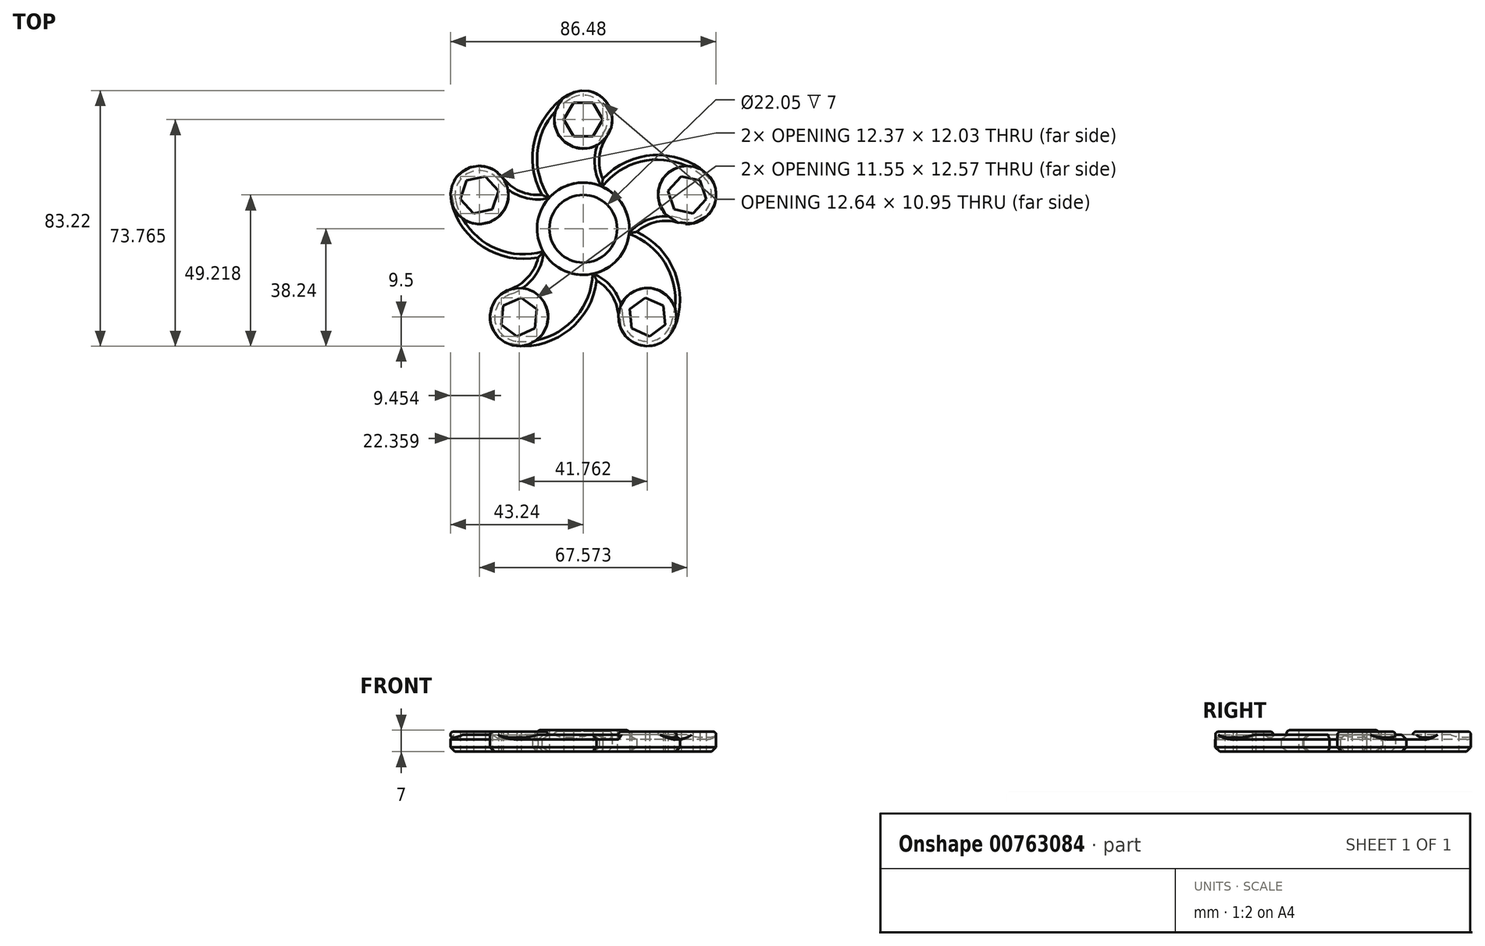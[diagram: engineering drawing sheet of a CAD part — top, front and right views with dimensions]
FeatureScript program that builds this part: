
annotation { "Feature Type Name" : "Feature", "Feature Type Description" : "" }
export const myFeature = defineFeature(function(context is Context, id is Id, definition is map)
    precondition{}
    {
        {
            var Q0;
            Q0=qCreatedBy(makeId("Top.planeOp"),FACE);
            var sketch = newSketch(context, id + "F0", { "sketchPlane" : qUnion([Q0])});
            skCircle(sketch, "E0", {"center": v(0, 0) * mm, "radius": 11.03 * mm});
            skCircle(sketch, "E1", {"center": v(0, 0) * mm, "radius": 15 * mm});
            skCircle(sketch, "E2.cCircle", {"center": v(0, 35.52) * mm, "radius": 5.47 * mm, "construction": true});
            skLineSegment(sketch, "E2.0", {"start": v(3.16, 30.05) * mm, "end": v(-3.16, 30.05) * mm});
            skLineSegment(sketch, "E2.1", {"start": v(-3.16, 30.05) * mm, "end": v(-6.32, 35.52) * mm});
            skLineSegment(sketch, "E2.2", {"start": v(-6.32, 35.52) * mm, "end": v(-3.16, 41) * mm});
            skLineSegment(sketch, "E2.3", {"start": v(-3.16, 41) * mm, "end": v(3.16, 41) * mm});
            skLineSegment(sketch, "E2.4", {"start": v(3.16, 41) * mm, "end": v(6.32, 35.52) * mm});
            skLineSegment(sketch, "E2.5", {"start": v(6.32, 35.52) * mm, "end": v(3.16, 30.05) * mm});
            skPoint(sketch, "E2.0.midPoint", {"position": v(0, 30.05) * mm});
            skCircle(sketch, "E3.1.0", {"center": v(33.79, 10.98) * mm, "radius": 5.47 * mm, "construction": true});
            skLineSegment(sketch, "E3.1.1", {"start": v(38.02, 15.68) * mm, "end": v(39.97, 9.66) * mm});
            skLineSegment(sketch, "E3.1.2", {"start": v(39.97, 9.66) * mm, "end": v(35.74, 4.97) * mm});
            skLineSegment(sketch, "E3.1.3", {"start": v(35.74, 4.97) * mm, "end": v(29.56, 6.28) * mm});
            skPoint(sketch, "E3.1.4", {"position": v(28.58, 9.29) * mm});
            skLineSegment(sketch, "E3.1.5", {"start": v(29.56, 6.28) * mm, "end": v(27.6, 12.3) * mm});
            skLineSegment(sketch, "E3.1.6", {"start": v(27.6, 12.3) * mm, "end": v(31.83, 17) * mm});
            skLineSegment(sketch, "E3.1.7", {"start": v(31.83, 17) * mm, "end": v(38.02, 15.68) * mm});
            skCircle(sketch, "E3.2.0", {"center": v(20.88, -28.74) * mm, "radius": 5.47 * mm, "construction": true});
            skLineSegment(sketch, "E3.2.1", {"start": v(26.66, -31.31) * mm, "end": v(21.54, -35.03) * mm});
            skLineSegment(sketch, "E3.2.2", {"start": v(21.54, -35.03) * mm, "end": v(15.77, -32.46) * mm});
            skLineSegment(sketch, "E3.2.3", {"start": v(15.77, -32.46) * mm, "end": v(15.1, -26.17) * mm});
            skPoint(sketch, "E3.2.4", {"position": v(17.66, -24.31) * mm});
            skLineSegment(sketch, "E3.2.5", {"start": v(15.1, -26.17) * mm, "end": v(20.22, -22.45) * mm});
            skLineSegment(sketch, "E3.2.6", {"start": v(20.22, -22.45) * mm, "end": v(26, -25.02) * mm});
            skLineSegment(sketch, "E3.2.7", {"start": v(26, -25.02) * mm, "end": v(26.66, -31.31) * mm});
            skCircle(sketch, "E3.3.0", {"center": v(-20.88, -28.74) * mm, "radius": 5.47 * mm, "construction": true});
            skLineSegment(sketch, "E3.3.1", {"start": v(-21.54, -35.03) * mm, "end": v(-26.66, -31.31) * mm});
            skLineSegment(sketch, "E3.3.2", {"start": v(-26.66, -31.31) * mm, "end": v(-26, -25.02) * mm});
            skLineSegment(sketch, "E3.3.3", {"start": v(-26, -25.02) * mm, "end": v(-20.22, -22.45) * mm});
            skPoint(sketch, "E3.3.4", {"position": v(-17.66, -24.31) * mm});
            skLineSegment(sketch, "E3.3.5", {"start": v(-20.22, -22.45) * mm, "end": v(-15.1, -26.17) * mm});
            skLineSegment(sketch, "E3.3.6", {"start": v(-15.1, -26.17) * mm, "end": v(-15.77, -32.46) * mm});
            skLineSegment(sketch, "E3.3.7", {"start": v(-15.77, -32.46) * mm, "end": v(-21.54, -35.03) * mm});
            skCircle(sketch, "E3.4.0", {"center": v(-33.79, 10.98) * mm, "radius": 5.47 * mm, "construction": true});
            skLineSegment(sketch, "E3.4.1", {"start": v(-39.97, 9.66) * mm, "end": v(-38.02, 15.68) * mm});
            skLineSegment(sketch, "E3.4.2", {"start": v(-38.02, 15.68) * mm, "end": v(-31.83, 17) * mm});
            skLineSegment(sketch, "E3.4.3", {"start": v(-31.83, 17) * mm, "end": v(-27.6, 12.3) * mm});
            skPoint(sketch, "E3.4.4", {"position": v(-28.58, 9.29) * mm});
            skLineSegment(sketch, "E3.4.5", {"start": v(-27.6, 12.3) * mm, "end": v(-29.56, 6.28) * mm});
            skLineSegment(sketch, "E3.4.6", {"start": v(-29.56, 6.28) * mm, "end": v(-35.74, 4.97) * mm});
            skLineSegment(sketch, "E3.4.7", {"start": v(-35.74, 4.97) * mm, "end": v(-39.97, 9.66) * mm});
            skLineSegment(sketch, "E3.anchor1", {"start": v(0, 0) * mm, "end": v(0, 30.05) * mm, "construction": true});
            skLineSegment(sketch, "E3.anchor2", {"start": v(0, 0) * mm, "end": v(-28.58, 9.29) * mm, "construction": true});
            skLineSegment(sketch, "E4", {"start": v(0, 0) * mm, "end": v(33.79, 10.98) * mm, "construction": true});
            skLineSegment(sketch, "E5", {"start": v(0, 0) * mm, "end": v(-20.88, -28.74) * mm, "construction": true});
            skLineSegment(sketch, "E6", {"start": v(20.88, -28.74) * mm, "end": v(0, 0) * mm, "construction": true});
            skCircle(sketch, "E7", {"center": v(0, 35.52) * mm, "radius": 9.45 * mm});
            skCircle(sketch, "E8.1.0", {"center": v(33.79, 10.98) * mm, "radius": 9.45 * mm});
            skCircle(sketch, "E8.2.0", {"center": v(20.88, -28.74) * mm, "radius": 9.45 * mm});
            skCircle(sketch, "E8.3.0", {"center": v(-20.88, -28.74) * mm, "radius": 9.45 * mm});
            skCircle(sketch, "E8.4.0", {"center": v(-33.79, 10.98) * mm, "radius": 9.45 * mm});
            skLineSegment(sketch, "E8.anchor1", {"start": v(0, 0) * mm, "end": v(0, 35.52) * mm, "construction": true});
            skLineSegment(sketch, "E8.anchor2", {"start": v(0, 0) * mm, "end": v(-33.79, 10.98) * mm, "construction": true});
            skArc(sketch, "E9", {"start": v(-4.94, 43.58) * mm, "mid": v(-15.73, 29.03) * mm, "end": v(-13.45, 11.07) * mm});
            skArc(sketch, "E10", {"start": v(7.76, 30.13) * mm, "mid": v(5.26, 23.35) * mm, "end": v(6.37, 16.21) * mm});
            skArc(sketch, "E11.1.0", {"start": v(-42.97, 8.76) * mm, "mid": v(-32.47, -6) * mm, "end": v(-14.68, -9.38) * mm});
            skArc(sketch, "E11.1.1", {"start": v(-26.26, 16.7) * mm, "mid": v(-20.59, 12.22) * mm, "end": v(-13.45, 11.07) * mm});
            skArc(sketch, "E11.2.0", {"start": v(-21.62, -38.16) * mm, "mid": v(-4.34, -32.73) * mm, "end": v(4.38, -16.86) * mm});
            skArc(sketch, "E11.2.1", {"start": v(-23.99, -19.82) * mm, "mid": v(-17.98, -15.8) * mm, "end": v(-14.68, -9.38) * mm});
            skArc(sketch, "E11.3.0", {"start": v(29.61, -32.35) * mm, "mid": v(29.8, -14.24) * mm, "end": v(17.39, -1.04) * mm});
            skArc(sketch, "E11.3.1", {"start": v(11.43, -28.94) * mm, "mid": v(9.47, -21.98) * mm, "end": v(4.38, -16.86) * mm});
            skArc(sketch, "E11.4.0", {"start": v(39.92, 18.17) * mm, "mid": v(22.75, 23.93) * mm, "end": v(6.37, 16.21) * mm});
            skArc(sketch, "E11.4.1", {"start": v(31.05, 1.93) * mm, "mid": v(23.84, 2.22) * mm, "end": v(17.39, -1.04) * mm});
            skPoint(sketch, "E12.orphan", {"position": v(10, 11.19) * mm});
            skPoint(sketch, "E13.orphan", {"position": v(4.72, 14.24) * mm});
            skPoint(sketch, "E14.orphan", {"position": v(15, -0.09) * mm});
            skPoint(sketch, "E15.orphan", {"position": v(13.73, -6.04) * mm});
            skPoint(sketch, "E16.orphan", {"position": v(4.55, -14.3) * mm});
            skPoint(sketch, "E17.orphan", {"position": v(-1.5, -14.92) * mm});
            skPoint(sketch, "E18.orphan", {"position": v(-12.19, -8.75) * mm});
            skPoint(sketch, "E19.orphan", {"position": v(-14.66, -3.18) * mm});
            skPoint(sketch, "E20.orphan", {"position": v(-7.55, 12.96) * mm});
            skPoint(sketch, "E21.orphan", {"position": v(-12.08, 8.89) * mm});
            skSolve(sketch);
        }
        {
            var Q0;
            Q0=makeQuery(id+"F0.imprint","IMPRINT",FACE,{"disambiguationData":[TD([[makeQuery(id+"F0.imprint","IMPRINT",EDGE,{"derivedFrom":sQuery(id+"F0.wireOp",EDGE,"E0")}),-1.0]])]});
            extrude(context, id + "F1", {"entities" : qUnion([Q0]), "depth" : 3.5 * mm, "offsetDistance" : 25 * mm, "hasSecondDirection" : true, "secondDirectionOppositeDirection" : true, "secondDirectionDepth" : 3.5 * mm});
        }
        {
            var Q0;
            Q0=makeQuery(id+"F0.imprint","IMPRINT",FACE,{"disambiguationData":[TD([[makeQuery(id+"F0.imprint","IMPRINT",EDGE,{"derivedFrom":sQuery(id+"F0.wireOp",EDGE,"E1")}),-1.0]])]});
            extrude(context, id + "F2", {"entities" : qUnion([Q0]), "operationType" : NewBodyOperationType.ADD, "depth" : 2 * mm, "offsetDistance" : 25 * mm, "hasSecondDirection" : true, "secondDirectionOppositeDirection" : true, "secondDirectionDepth" : 3.5 * mm});
        }
        {
            var Q0;
            Q0=makeQuery(id+"F0.imprint","IMPRINT",FACE,{"disambiguationData":[TD([[makeQuery(id+"F0.imprint","IMPRINT",EDGE,{"derivedFrom":sQuery(id+"F0.wireOp",EDGE,"E3.1.1")}),1.0]])]});
            var Q1;
            Q1=makeQuery(id+"F0.imprint","IMPRINT",FACE,{"disambiguationData":[TD([[makeQuery(id+"F0.imprint","IMPRINT",EDGE,{"derivedFrom":sQuery(id+"F0.wireOp",EDGE,"E3.4.1")}),1.0]])]});
            var Q2;
            Q2=makeQuery(id+"F0.imprint","IMPRINT",FACE,{"disambiguationData":[TD([[makeQuery(id+"F0.imprint","IMPRINT",EDGE,{"derivedFrom":sQuery(id+"F0.wireOp",EDGE,"E2.0")}),1.0]])]});
            var Q3;
            Q3=makeQuery(id+"F0.imprint","IMPRINT",FACE,{"disambiguationData":[TD([[makeQuery(id+"F0.imprint","IMPRINT",EDGE,{"derivedFrom":sQuery(id+"F0.wireOp",EDGE,"E3.3.1")}),1.0]])]});
            var Q4;
            Q4=makeQuery(id+"F0.imprint","IMPRINT",FACE,{"disambiguationData":[TD([[makeQuery(id+"F0.imprint","IMPRINT",EDGE,{"derivedFrom":sQuery(id+"F0.wireOp",EDGE,"E3.2.1")}),1.0]])]});
            extrude(context, id + "F3", {"entities" : qUnion([Q0, Q1, Q2, Q3, Q4]), "operationType" : NewBodyOperationType.ADD, "depth" : 3 * mm, "offsetDistance" : 25 * mm, "hasSecondDirection" : true, "secondDirectionOppositeDirection" : true, "secondDirectionDepth" : 3.5 * mm});
        }
        {
            var Q0;
            Q0=makeQuery(id+"F3.opExtrude","CAP_EDGE",EDGE,{"disambiguationData":[OSD([sQuery(id+"F0.wireOp",EDGE,"E8.2.0")])],"isStart":false});
            var Q1;
            Q1=makeQuery(id+"F3.opExtrude","CAP_EDGE",EDGE,{"disambiguationData":[OSD([sQuery(id+"F0.wireOp",EDGE,"E8.3.0")])],"isStart":false});
            var Q2;
            Q2=makeQuery(id+"F1.opExtrude","CAP_EDGE",EDGE,{"disambiguationData":[OSD([sQuery(id+"F0.wireOp",EDGE,"E1")])],"isStart":false});
            var Q3;
            Q3=makeQuery(id+"F3.opExtrude","CAP_EDGE",EDGE,{"disambiguationData":[OSD([sQuery(id+"F0.wireOp",EDGE,"E8.1.0")])],"isStart":false});
            var Q4;
            Q4=makeQuery(id+"F3.opExtrude","CAP_EDGE",EDGE,{"disambiguationData":[OSD([sQuery(id+"F0.wireOp",EDGE,"E7")])],"isStart":false});
            var Q5;
            Q5=makeQuery(id+"F3.opExtrude","CAP_EDGE",EDGE,{"disambiguationData":[OSD([sQuery(id+"F0.wireOp",EDGE,"E8.4.0")])],"isStart":false});
            fillet(context, id + "F4", {"entities" : qUnion([Q0, Q1, Q2, Q3, Q4, Q5]), "radius" : 1 * mm, "tangentPropagation" : true, "allowEdgeOverflow" : false});
        }
        {
            var Q0;
            Q0=makeQuery(id+"F2.opExtrude","CAP_EDGE",EDGE,{"disambiguationData":[OSD([sQuery(id+"F0.wireOp",EDGE,"E11.4.0")])],"isStart":true});
            var Q1;
            Q1=makeQuery(id+"F2.opExtrude","CAP_EDGE",EDGE,{"disambiguationData":[OSD([sQuery(id+"F0.wireOp",EDGE,"E10")])],"isStart":true});
            var Q2;
            Q2=makeQuery(id+"F3.opExtrude","CAP_EDGE",EDGE,{"disambiguationData":[OSD([sQuery(id+"F0.wireOp",EDGE,"E7")])],"isStart":true});
            var Q3;
            Q3=makeQuery(id+"F2.opExtrude","CAP_EDGE",EDGE,{"disambiguationData":[OSD([sQuery(id+"F0.wireOp",EDGE,"E9")])],"isStart":true});
            var Q4;
            Q4=makeQuery(id+"F2.opExtrude","CAP_EDGE",EDGE,{"disambiguationData":[OSD([sQuery(id+"F0.wireOp",EDGE,"E11.1.1")])],"isStart":true});
            var Q5;
            Q5=makeQuery(id+"F3.opExtrude","CAP_EDGE",EDGE,{"disambiguationData":[OSD([sQuery(id+"F0.wireOp",EDGE,"E8.4.0")])],"isStart":true});
            var Q6;
            Q6=makeQuery(id+"F2.opExtrude","CAP_EDGE",EDGE,{"disambiguationData":[OSD([sQuery(id+"F0.wireOp",EDGE,"E11.1.0")])],"isStart":true});
            var Q7;
            Q7=makeQuery(id+"F2.opExtrude","CAP_EDGE",EDGE,{"disambiguationData":[OSD([sQuery(id+"F0.wireOp",EDGE,"E11.2.1")])],"isStart":true});
            var Q8;
            Q8=makeQuery(id+"F3.opExtrude","CAP_EDGE",EDGE,{"disambiguationData":[OSD([sQuery(id+"F0.wireOp",EDGE,"E8.3.0")])],"isStart":true});
            var Q9;
            Q9=makeQuery(id+"F2.opExtrude","CAP_EDGE",EDGE,{"disambiguationData":[OSD([sQuery(id+"F0.wireOp",EDGE,"E11.2.0")])],"isStart":true});
            var Q10;
            Q10=makeQuery(id+"F2.opExtrude","CAP_EDGE",EDGE,{"disambiguationData":[OSD([sQuery(id+"F0.wireOp",EDGE,"E11.3.1")])],"isStart":true});
            var Q11;
            Q11=makeQuery(id+"F3.opExtrude","CAP_EDGE",EDGE,{"disambiguationData":[OSD([sQuery(id+"F0.wireOp",EDGE,"E8.2.0")])],"isStart":true});
            var Q12;
            Q12=makeQuery(id+"F2.opExtrude","CAP_EDGE",EDGE,{"disambiguationData":[OSD([sQuery(id+"F0.wireOp",EDGE,"E11.3.0")])],"isStart":true});
            var Q13;
            Q13=makeQuery(id+"F2.opExtrude","CAP_EDGE",EDGE,{"disambiguationData":[OSD([sQuery(id+"F0.wireOp",EDGE,"E11.4.1")])],"isStart":true});
            var Q14;
            Q14=makeQuery(id+"F3.opExtrude","CAP_EDGE",EDGE,{"disambiguationData":[OSD([sQuery(id+"F0.wireOp",EDGE,"E8.1.0")])],"isStart":true});
            chamfer(context, id + "F5", {"entities" : qUnion([Q0, Q1, Q2, Q3, Q4, Q5, Q6, Q7, Q8, Q9, Q10, Q11, Q12, Q13, Q14]), "width" : 1.5 * mm, "tangentPropagation" : true});
        }
        {
            var Q0;
            Q0=makeQuery(id+"F2.opExtrude","CAP_EDGE",EDGE,{"disambiguationData":[OSD([sQuery(id+"F0.wireOp",EDGE,"E11.1.1")])],"isStart":false});
            var Q1;
            Q1=makeQuery(id+"F2.opExtrude","CAP_EDGE",EDGE,{"disambiguationData":[OSD([sQuery(id+"F0.wireOp",EDGE,"E11.1.0")])],"isStart":false});
            var Q2;
            Q2=makeQuery(id+"F2.opExtrude","CAP_EDGE",EDGE,{"disambiguationData":[OSD([sQuery(id+"F0.wireOp",EDGE,"E11.2.1")])],"isStart":false});
            var Q3;
            Q3=makeQuery(id+"F2.opExtrude","CAP_EDGE",EDGE,{"disambiguationData":[OSD([sQuery(id+"F0.wireOp",EDGE,"E9")])],"isStart":false});
            var Q4;
            Q4=makeQuery(id+"F2.opExtrude","CAP_EDGE",EDGE,{"disambiguationData":[OSD([sQuery(id+"F0.wireOp",EDGE,"E10")])],"isStart":false});
            var Q5;
            Q5=makeQuery(id+"F2.opExtrude","CAP_EDGE",EDGE,{"disambiguationData":[OSD([sQuery(id+"F0.wireOp",EDGE,"E11.4.0")])],"isStart":false});
            var Q6;
            Q6=makeQuery(id+"F2.opExtrude","CAP_EDGE",EDGE,{"disambiguationData":[OSD([sQuery(id+"F0.wireOp",EDGE,"E11.4.1")])],"isStart":false});
            var Q7;
            Q7=makeQuery(id+"F2.opExtrude","CAP_EDGE",EDGE,{"disambiguationData":[OSD([sQuery(id+"F0.wireOp",EDGE,"E11.3.0")])],"isStart":false});
            var Q8;
            Q8=makeQuery(id+"F2.opExtrude","CAP_EDGE",EDGE,{"disambiguationData":[OSD([sQuery(id+"F0.wireOp",EDGE,"E11.3.1")])],"isStart":false});
            var Q9;
            Q9=makeQuery(id+"F2.opExtrude","CAP_EDGE",EDGE,{"disambiguationData":[OSD([sQuery(id+"F0.wireOp",EDGE,"E11.2.0")])],"isStart":false});
            chamfer(context, id + "F6", {"entities" : qUnion([Q0, Q1, Q2, Q3, Q4, Q5, Q6, Q7, Q8, Q9]), "width" : 1.5 * mm, "tangentPropagation" : true});
        }
    });
